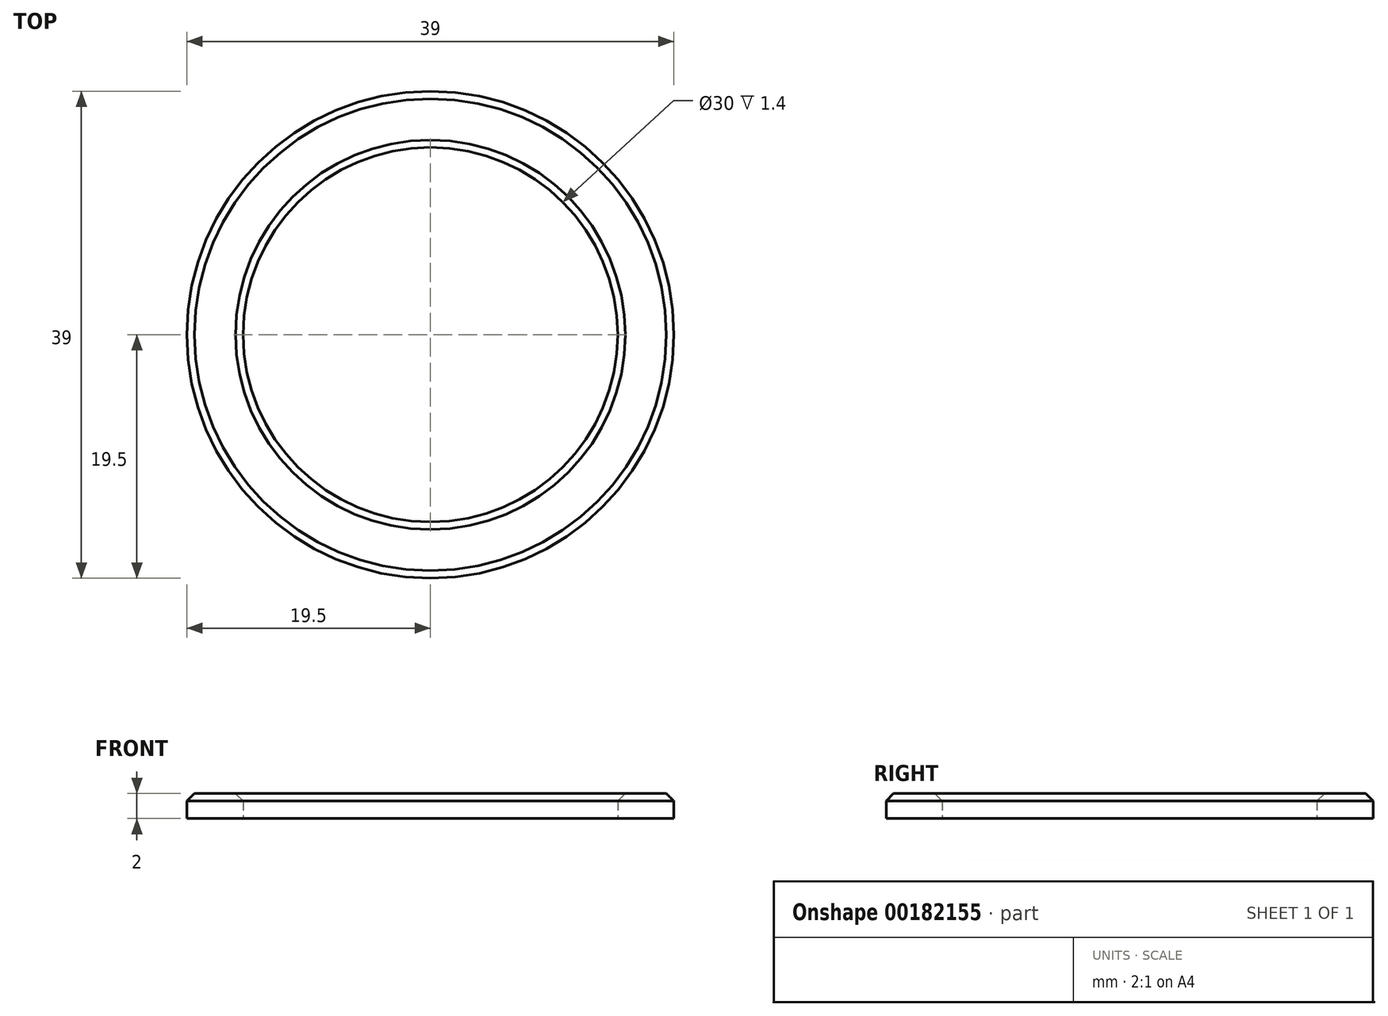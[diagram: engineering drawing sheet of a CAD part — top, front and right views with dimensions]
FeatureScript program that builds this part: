
annotation { "Feature Type Name" : "Feature", "Feature Type Description" : "" }
export const myFeature = defineFeature(function(context is Context, id is Id, definition is map)
    precondition{}
    {
        {
            var Q0;
            Q0=qCreatedBy(makeId("Top.planeOp"),FACE);
            var sketch = newSketch(context, id + "F0", { "sketchPlane" : qUnion([Q0])});
            skCircle(sketch, "E0", {"center": v(0, 0) * mm, "radius": 19.5 * mm});
            skCircle(sketch, "E1", {"center": v(0, 0) * mm, "radius": 15 * mm});
            skSolve(sketch);
        }
        {
            var Q0;
            Q0 = qSketchRegion(id + "F0", true);
            extrude(context, id + "F1", {"entities" : qUnion([Q0]), "depth" : 2 * mm});
        }
        {
            var Q0;
            Q0=makeQuery(id+"F1.opExtrude","CAP_EDGE",EDGE,{"disambiguationData":[OSD([sQuery(id+"F0.wireOp",EDGE,"E0")])],"isStart":false});
            var Q1;
            Q1=makeQuery(id+"F1.opExtrude","CAP_EDGE",EDGE,{"disambiguationData":[OSD([sQuery(id+"F0.wireOp",EDGE,"E1")])],"isStart":false});
            chamfer(context, id + "F2", {"entities" : qUnion([Q0, Q1]), "width" : 0.6 * mm, "tangentPropagation" : true});
        }
    });
